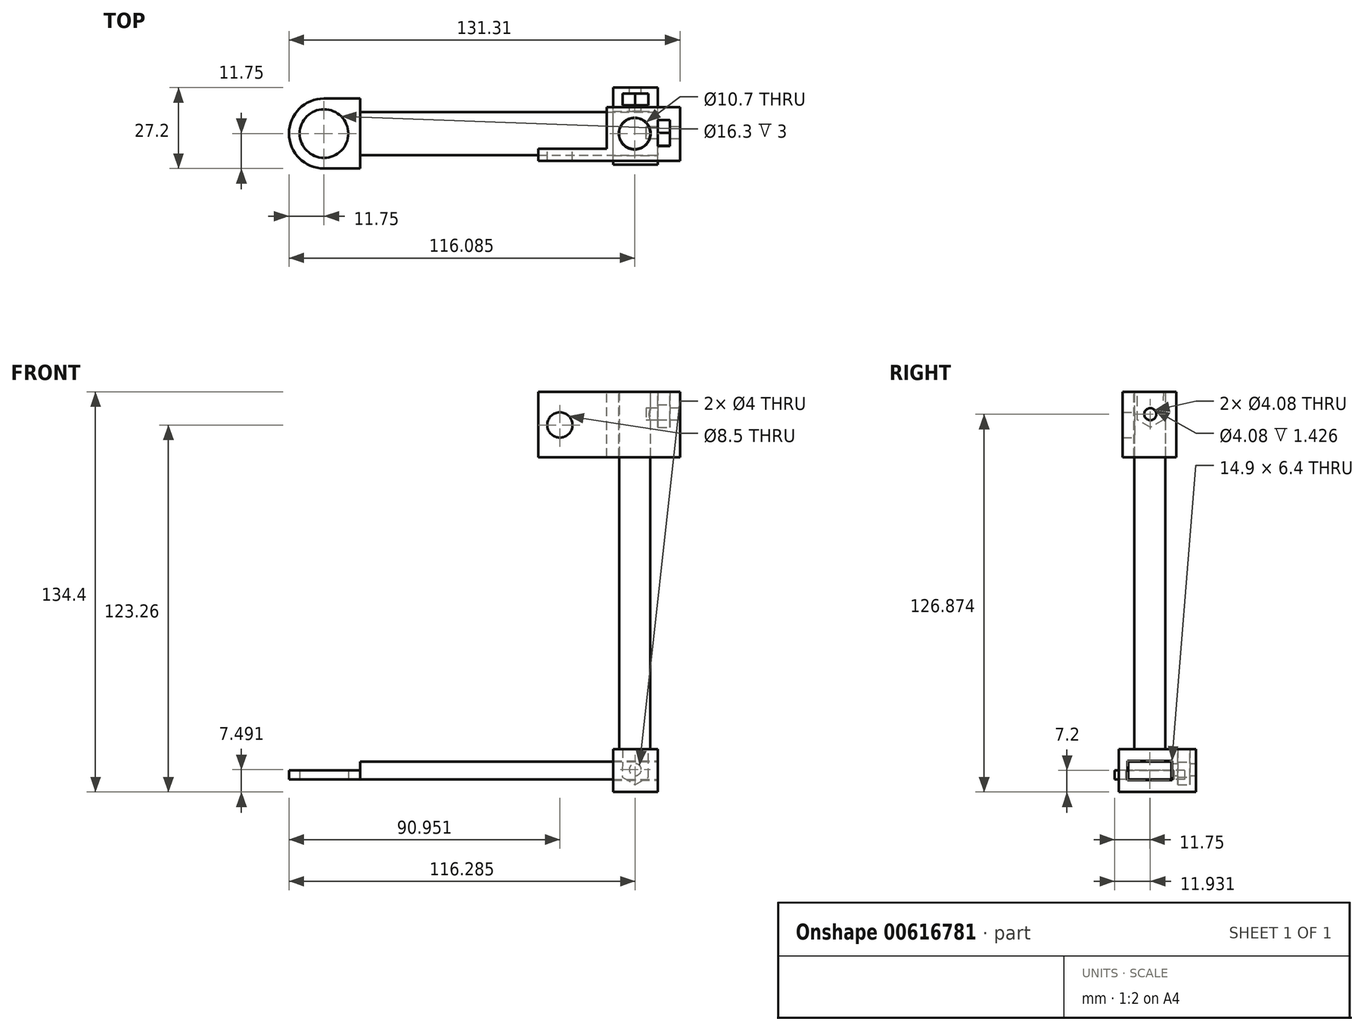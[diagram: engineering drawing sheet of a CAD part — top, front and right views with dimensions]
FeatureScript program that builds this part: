
annotation { "Feature Type Name" : "Feature", "Feature Type Description" : "" }
export const myFeature = defineFeature(function(context is Context, id is Id, definition is map)
    precondition{}
    {
        {
            var Q0;
            Q0=qCreatedBy(makeId("Top.planeOp"),FACE);
            var sketch = newSketch(context, id + "F0", { "sketchPlane" : qUnion([Q0])});
            skCircle(sketch, "E0", {"center": v(0, 0) * mm, "radius": 8.15 * mm});
            skArc(sketch, "E1", {"start": v(0, 11.75) * mm, "mid": v(-11.75, 0) * mm, "end": v(0, -11.75) * mm});
            skLineSegment(sketch, "E2.bottom", {"start": v(0, 11.75) * mm, "end": v(12.1, 11.75) * mm});
            skLineSegment(sketch, "E2.top", {"start": v(0, -11.75) * mm, "end": v(12.1, -11.75) * mm});
            skLineSegment(sketch, "E3", {"start": v(12.1, 11.75) * mm, "end": v(12.1, -11.75) * mm});
            skSolve(sketch);
        }
        {
            var Q0;
            Q0=makeQuery(id+"F0.imprint","IMPRINT",FACE,{"disambiguationData":[TD([[makeQuery(id+"F0.imprint","IMPRINT",EDGE,{"derivedFrom":sQuery(id+"F0.wireOp",EDGE,"E0")}),-1.0]])]});
            extrude(context, id + "F1", {"entities" : qUnion([Q0]), "depth" : 3 * mm, "offsetDistance" : 25 * mm});
        }
        {
            var Q0;
            Q0=qCreatedBy(makeId("Top.planeOp"),FACE);
            var sketch = newSketch(context, id + "F2", { "sketchPlane" : qUnion([Q0])});
            skLineSegment(sketch, "E4.bottom", {"start": v(12.1, 7.25) * mm, "end": v(112.1, 7.25) * mm});
            skLineSegment(sketch, "E4.top", {"start": v(12.1, -7.25) * mm, "end": v(112.1, -7.25) * mm});
            skLineSegment(sketch, "E4.left", {"start": v(12.1, 7.25) * mm, "end": v(12.1, -7.25) * mm});
            skLineSegment(sketch, "E4.right", {"start": v(112.1, 7.25) * mm, "end": v(112.1, -7.25) * mm});
            skSolve(sketch);
        }
        {
            var Q0;
            Q0=makeQuery(id+"F2.imprint","IMPRINT",FACE,{"disambiguationData":[TD([[makeQuery(id+"F2.imprint","IMPRINT",EDGE,{"derivedFrom":sQuery(id+"F2.wireOp",EDGE,"E4.bottom")}),-1.0]])]});
            extrude(context, id + "F3", {"entities" : qUnion([Q0]), "operationType" : NewBodyOperationType.ADD, "depth" : 6 * mm, "offsetDistance" : 25 * mm});
        }
        {
            var Q0;
            Q0=makeQuery(id+"F3.opExtrude","SWEPT_FACE",FACE,{"disambiguationData":[OSD([sQuery(id+"F2.wireOp",EDGE,"E4.right")])]});
            var sketch = newSketch(context, id + "F4", { "sketchPlane" : qUnion([Q0])});
            skLineSegment(sketch, "E5.bottom", {"start": v(-7.25, 0) * mm, "end": v(7.25, 0) * mm});
            skLineSegment(sketch, "E5.top", {"start": v(-7.25, 6) * mm, "end": v(7.25, 6) * mm});
            skLineSegment(sketch, "E5.left", {"start": v(-7.25, 0) * mm, "end": v(-7.25, 6) * mm});
            skLineSegment(sketch, "E5.right", {"start": v(7.25, 0) * mm, "end": v(7.25, 6) * mm});
            skLineSegment(sketch, "E6.0", {"start": v(-7.45, -0.2) * mm, "end": v(7.45, -0.2) * mm});
            skLineSegment(sketch, "E6.1", {"start": v(-7.45, 6.2) * mm, "end": v(-7.45, -0.2) * mm});
            skLineSegment(sketch, "E6.2", {"start": v(7.45, 6.2) * mm, "end": v(-7.45, 6.2) * mm});
            skLineSegment(sketch, "E6.3", {"start": v(7.45, -0.2) * mm, "end": v(7.45, 6.2) * mm});
            skLineSegment(sketch, "E7.bottom", {"start": v(-10.45, -4.2) * mm, "end": v(15.45, -4.2) * mm});
            skLineSegment(sketch, "E7.top", {"start": v(-10.45, 10.2) * mm, "end": v(15.45, 10.2) * mm});
            skLineSegment(sketch, "E7.left", {"start": v(-10.45, -4.2) * mm, "end": v(-10.45, 10.2) * mm});
            skLineSegment(sketch, "E7.right", {"start": v(15.45, -4.2) * mm, "end": v(15.45, 10.2) * mm});
            skSolve(sketch);
        }
        {
            var Q0;
            Q0=makeQuery(id+"F4.imprint","IMPRINT",FACE,{"disambiguationData":[TD([[makeQuery(id+"F4.imprint","IMPRINT",EDGE,{"derivedFrom":sQuery(id+"F4.wireOp",EDGE,"E6.0")}),-1.0]])]});
            extrude(context, id + "F5", {"entities" : qUnion([Q0]), "oppositeDirection" : true, "depth" : 15 * mm, "offsetDistance" : 25 * mm});
        }
        {
            var Q0;
            Q0=makeQuery(id+"F5.opExtrude","SWEPT_FACE",FACE,{"disambiguationData":[OSD([sQuery(id+"F4.wireOp",EDGE,"E7.right")])]});
            var sketch = newSketch(context, id + "F6", { "sketchPlane" : qUnion([Q0])});
            skLineSegment(sketch, "E8.0", {"start": v(-100.2, 0.8) * mm, "end": v(-104.52, -1.76) * mm});
            skLineSegment(sketch, "E8.1", {"start": v(-104.52, -1.76) * mm, "end": v(-108.9, 0.71) * mm});
            skLineSegment(sketch, "E8.2", {"start": v(-108.9, 0.71) * mm, "end": v(-108.94, 5.73) * mm});
            skLineSegment(sketch, "E8.5", {"start": v(-100.24, 5.82) * mm, "end": v(-100.2, 0.8) * mm});
            skPoint(sketch, "E8.0.midPoint", {"position": v(-102.36, -0.48) * mm});
            skLineSegment(sketch, "E9", {"start": v(-108.94, 5.73) * mm, "end": v(-108.94, 10.2) * mm});
            skLineSegment(sketch, "E10", {"start": v(-108.94, 10.2) * mm, "end": v(-100.23, 10.2) * mm});
            skLineSegment(sketch, "E11", {"start": v(-100.23, 10.2) * mm, "end": v(-100.24, 5.82) * mm});
            skSolve(sketch);
        }
        {
            var Q0;
            Q0=makeQuery(id+"F6.imprint","IMPRINT",FACE,{"disambiguationData":[TD([[makeQuery(id+"F6.imprint","IMPRINT",EDGE,{"derivedFrom":sQuery(id+"F6.wireOp",EDGE,"E8.0")}),-1.0]])]});
            extrude(context, id + "F7", {"entities" : qUnion([Q0]), "oppositeDirection" : true, "depth" : 4 * mm, "offsetDistance" : 25 * mm});
        }
        {
            var Q0;
            Q0=makeQuery(id+"F7.opExtrude","SWEPT_BODY",BODY,{"disambiguationData":[OSD([sQuery(id+"F6.wireOp",EDGE,"E8.0"),sQuery(id+"F6.wireOp",EDGE,"E8.1"),sQuery(id+"F6.wireOp",EDGE,"E8.2"),sQuery(id+"F6.wireOp",EDGE,"E8.5"),sQuery(id+"F6.wireOp",EDGE,"E9"),sQuery(id+"F6.wireOp",EDGE,"E10"),sQuery(id+"F6.wireOp",EDGE,"E11")])]});
            transform(context, id + "F8", {"entities" : qUnion([Q0]), "transformType" : TransformType.TRANSLATION_3D, "dx" : 0 * mm, "dy" : -2 * mm, "dz" : 0 * mm, "makeCopy" : false});
        }
        {
            var Q0;
            Q0=makeQuery(id+"F7.opExtrude","SWEPT_BODY",BODY,{"disambiguationData":[OSD([sQuery(id+"F6.wireOp",EDGE,"E8.0"),sQuery(id+"F6.wireOp",EDGE,"E8.1"),sQuery(id+"F6.wireOp",EDGE,"E8.2"),sQuery(id+"F6.wireOp",EDGE,"E8.5"),sQuery(id+"F6.wireOp",EDGE,"E9"),sQuery(id+"F6.wireOp",EDGE,"E10"),sQuery(id+"F6.wireOp",EDGE,"E11")])]});
            var Q1;
            Q1=makeQuery(id+"F5.opExtrude","SWEPT_BODY",BODY,{"disambiguationData":[OSD([sQuery(id+"F4.wireOp",EDGE,"E6.0"),sQuery(id+"F4.wireOp",EDGE,"E6.1"),sQuery(id+"F4.wireOp",EDGE,"E6.2"),sQuery(id+"F4.wireOp",EDGE,"E6.3"),sQuery(id+"F4.wireOp",EDGE,"E7.bottom"),sQuery(id+"F4.wireOp",EDGE,"E7.top"),sQuery(id+"F4.wireOp",EDGE,"E7.left"),sQuery(id+"F4.wireOp",EDGE,"E7.right")])]});
            booleanBodies(context, id + "F9", {"operationType" : BooleanOperationType.SUBTRACTION, "tools" : qUnion([Q0]), "targets" : qUnion([Q1])});
        }
        {
            var Q0;
            Q0=makeQuery(id+"F5.opExtrude","SWEPT_FACE",FACE,{"disambiguationData":[OSD([sQuery(id+"F4.wireOp",EDGE,"E7.right")])]});
            var sketch = newSketch(context, id + "F10", { "sketchPlane" : qUnion([Q0])});
            skCircle(sketch, "E12", {"center": v(-104.54, 3.3) * mm, "radius": 2 * mm});
            skSolve(sketch);
        }
        {
            var Q0;
            Q0 = qSketchRegion(id + "F10", true);
            extrude(context, id + "F11", {"entities" : qUnion([Q0]), "operationType" : NewBodyOperationType.REMOVE, "oppositeDirection" : true, "depth" : 8 * mm, "offsetDistance" : 25 * mm});
        }
        {
            var Q0;
            Q0=makeQuery(id+"F5.opExtrude","SWEPT_FACE",FACE,{"disambiguationData":[OSD([sQuery(id+"F4.wireOp",EDGE,"E7.top")])]});
            var sketch = newSketch(context, id + "F12", { "sketchPlane" : qUnion([Q0])});
            skCircle(sketch, "E13", {"center": v(104.33, 0) * mm, "radius": 5.25 * mm});
            skSolve(sketch);
        }
        {
            var Q0;
            Q0=makeQuery(id+"F12.imprint","IMPRINT",FACE,{"disambiguationData":[TD([[makeQuery(id+"F12.imprint","IMPRINT",EDGE,{"derivedFrom":sQuery(id+"F12.wireOp",EDGE,"E13")}),1.0]])]});
            var Q1;
            Q1=sQuery(id+"F12.wireOp",EDGE,"E13");
            extrude(context, id + "F13", {"entities" : qUnion([Q0]), "operationType" : NewBodyOperationType.ADD, "surfaceEntities" : qUnion([Q1]), "depth" : 120 * mm, "offsetDistance" : 25 * mm});
        }
        {
            var Q0;
            Q0=makeQuery(id+"F13.opExtrude","CAP_FACE",FACE,{"disambiguationData":[OSD([sQuery(id+"F12.wireOp",EDGE,"E13")])],"isStart":false});
            var sketch = newSketch(context, id + "F14", { "sketchPlane" : qUnion([Q0])});
            skCircle(sketch, "E14", {"center": v(104.33, 0) * mm, "radius": 5.35 * mm});
            skLineSegment(sketch, "E15.bottom", {"start": v(119.56, -9.13) * mm, "end": v(94.9, -9.13) * mm});
            skLineSegment(sketch, "E15.top", {"start": v(119.56, 8.9) * mm, "end": v(94.9, 8.9) * mm});
            skLineSegment(sketch, "E15.left", {"start": v(119.56, -9.13) * mm, "end": v(119.56, 8.9) * mm});
            skLineSegment(sketch, "E15.right", {"start": v(94.9, -9.13) * mm, "end": v(94.9, 8.9) * mm});
            skSolve(sketch);
        }
        {
            var Q0;
            Q0=makeQuery(id+"F14.imprint","IMPRINT",FACE,{"disambiguationData":[TD([[makeQuery(id+"F14.imprint","IMPRINT",EDGE,{"derivedFrom":sQuery(id+"F14.wireOp",EDGE,"E14")}),-1.0]])]});
            extrude(context, id + "F15", {"entities" : qUnion([Q0]), "oppositeDirection" : true, "depth" : 22 * mm, "offsetDistance" : 25 * mm});
        }
        {
            var Q0;
            Q0=makeQuery(id+"F15.opExtrude","SWEPT_FACE",FACE,{"disambiguationData":[OSD([sQuery(id+"F14.wireOp",EDGE,"E15.left")])]});
            var sketch = newSketch(context, id + "F16", { "sketchPlane" : qUnion([Q0])});
            skLineSegment(sketch, "E16.0", {"start": v(4.55, 120.8) * mm, "end": v(0.23, 118.26) * mm});
            skLineSegment(sketch, "E16.1", {"start": v(0.23, 118.26) * mm, "end": v(-4.15, 120.73) * mm});
            skLineSegment(sketch, "E16.2", {"start": v(-4.15, 120.73) * mm, "end": v(-4.2, 125.75) * mm});
            skLineSegment(sketch, "E16.5", {"start": v(4.5, 125.83) * mm, "end": v(4.55, 120.8) * mm});
            skPoint(sketch, "E16.0.midPoint", {"position": v(2.4, 119.53) * mm});
            skLineSegment(sketch, "E17", {"start": v(-4.2, 125.75) * mm, "end": v(-4.2, 130.22) * mm});
            skLineSegment(sketch, "E18", {"start": v(-4.2, 130.22) * mm, "end": v(4.52, 130.22) * mm});
            skLineSegment(sketch, "E19", {"start": v(4.52, 130.22) * mm, "end": v(4.5, 125.83) * mm});
            skSolve(sketch);
        }
        {
            var Q0;
            Q0=makeQuery(id+"F16.imprint","IMPRINT",FACE,{"disambiguationData":[TD([[makeQuery(id+"F16.imprint","IMPRINT",EDGE,{"derivedFrom":sQuery(id+"F16.wireOp",EDGE,"E16.0")}),-1.0]])]});
            extrude(context, id + "F17", {"entities" : qUnion([Q0]), "oppositeDirection" : true, "depth" : 4 * mm, "offsetDistance" : 25 * mm});
        }
        {
            var Q0;
            Q0=makeQuery(id+"F17.opExtrude","SWEPT_BODY",BODY,{"disambiguationData":[OSD([sQuery(id+"F14.wireOp",EDGE,"E15.left"),sQuery(id+"F16.wireOp",EDGE,"E16.0"),sQuery(id+"F16.wireOp",EDGE,"E16.1"),sQuery(id+"F16.wireOp",EDGE,"E16.2"),sQuery(id+"F16.wireOp",EDGE,"E16.5"),sQuery(id+"F16.wireOp",EDGE,"E17"),sQuery(id+"F16.wireOp",EDGE,"E19")])]});
            transform(context, id + "F18", {"entities" : qUnion([Q0]), "transformType" : TransformType.TRANSLATION_3D, "dx" : -3.4 * mm, "dy" : 0 * mm, "dz" : 0 * mm, "makeCopy" : false});
        }
        {
            var Q0;
            Q0=makeQuery(id+"F17.opExtrude","SWEPT_BODY",BODY,{"disambiguationData":[OSD([sQuery(id+"F14.wireOp",EDGE,"E15.left"),sQuery(id+"F16.wireOp",EDGE,"E16.0"),sQuery(id+"F16.wireOp",EDGE,"E16.1"),sQuery(id+"F16.wireOp",EDGE,"E16.2"),sQuery(id+"F16.wireOp",EDGE,"E16.5"),sQuery(id+"F16.wireOp",EDGE,"E17"),sQuery(id+"F16.wireOp",EDGE,"E19")])]});
            var Q1;
            Q1=makeQuery(id+"F15.opExtrude","SWEPT_BODY",BODY,{"disambiguationData":[OSD([sQuery(id+"F14.wireOp",EDGE,"E14"),sQuery(id+"F14.wireOp",EDGE,"E15.bottom"),sQuery(id+"F14.wireOp",EDGE,"E15.top"),sQuery(id+"F14.wireOp",EDGE,"E15.left"),sQuery(id+"F14.wireOp",EDGE,"E15.right")])]});
            booleanBodies(context, id + "F19", {"operationType" : BooleanOperationType.SUBTRACTION, "tools" : qUnion([Q0]), "targets" : qUnion([Q1])});
        }
        {
            var Q0;
            Q0=makeQuery(id+"F15.opExtrude","SWEPT_FACE",FACE,{"disambiguationData":[OSD([sQuery(id+"F14.wireOp",EDGE,"E15.right")])]});
            var sketch = newSketch(context, id + "F20", { "sketchPlane" : qUnion([Q0])});
            skLineSegment(sketch, "E20.bottom", {"start": v(9.13, 108.2) * mm, "end": v(5.13, 108.2) * mm});
            skLineSegment(sketch, "E20.top", {"start": v(9.13, 130.2) * mm, "end": v(5.13, 130.2) * mm});
            skLineSegment(sketch, "E20.left", {"start": v(9.13, 108.2) * mm, "end": v(9.13, 130.2) * mm});
            skLineSegment(sketch, "E20.right", {"start": v(5.13, 108.2) * mm, "end": v(5.13, 130.2) * mm});
            skSolve(sketch);
        }
        {
            var Q0;
            Q0=makeQuery(id+"F20.imprint","IMPRINT",FACE,{"disambiguationData":[TD([[makeQuery(id+"F20.imprint","IMPRINT",EDGE,{"derivedFrom":sQuery(id+"F20.wireOp",EDGE,"E20.bottom")}),-1.0]])]});
            extrude(context, id + "F21", {"entities" : qUnion([Q0]), "operationType" : NewBodyOperationType.ADD, "depth" : 23 * mm, "offsetDistance" : 25 * mm});
        }
        {
            var Q0;
            Q0=makeQuery(id+"F21.opExtrude","SWEPT_FACE",FACE,{"disambiguationData":[OSD([sQuery(id+"F20.wireOp",EDGE,"E20.right")])]});
            var sketch = newSketch(context, id + "F22", { "sketchPlane" : qUnion([Q0])});
            skCircle(sketch, "E21", {"center": v(-79.2, 119.06) * mm, "radius": 4.25 * mm});
            skSolve(sketch);
        }
        {
            var Q0;
            Q0 = qSketchRegion(id + "F22", true);
            extrude(context, id + "F23", {"entities" : qUnion([Q0]), "operationType" : NewBodyOperationType.REMOVE, "oppositeDirection" : true, "depth" : 6.9 * mm, "offsetDistance" : 25 * mm});
        }
        {
            var Q0;
            Q0=makeQuery(id+"F19.opBoolean","COPY",FACE,{"derivedFrom":makeQuery(id+"F17.opExtrude","CAP_FACE",FACE,{"disambiguationData":[OSD([sQuery(id+"F14.wireOp",EDGE,"E15.left"),sQuery(id+"F16.wireOp",EDGE,"E16.0"),sQuery(id+"F16.wireOp",EDGE,"E16.1"),sQuery(id+"F16.wireOp",EDGE,"E16.2"),sQuery(id+"F16.wireOp",EDGE,"E16.5"),sQuery(id+"F16.wireOp",EDGE,"E17"),sQuery(id+"F16.wireOp",EDGE,"E19")])],"isStart":true})});
            var sketch = newSketch(context, id + "F24", { "sketchPlane" : qUnion([Q0])});
            skCircle(sketch, "E22", {"center": v(-0.18, 122.67) * mm, "radius": 2.04 * mm});
            skSolve(sketch);
        }
        {
            var Q0;
            Q0 = qSketchRegion(id + "F24", true);
            extrude(context, id + "F25", {"entities" : qUnion([Q0]), "operationType" : NewBodyOperationType.REMOVE, "endBound" : BoundingType.SYMMETRIC, "oppositeDirection" : true, "depth" : 16 * mm, "offsetDistance" : 25 * mm});
        }
    });
